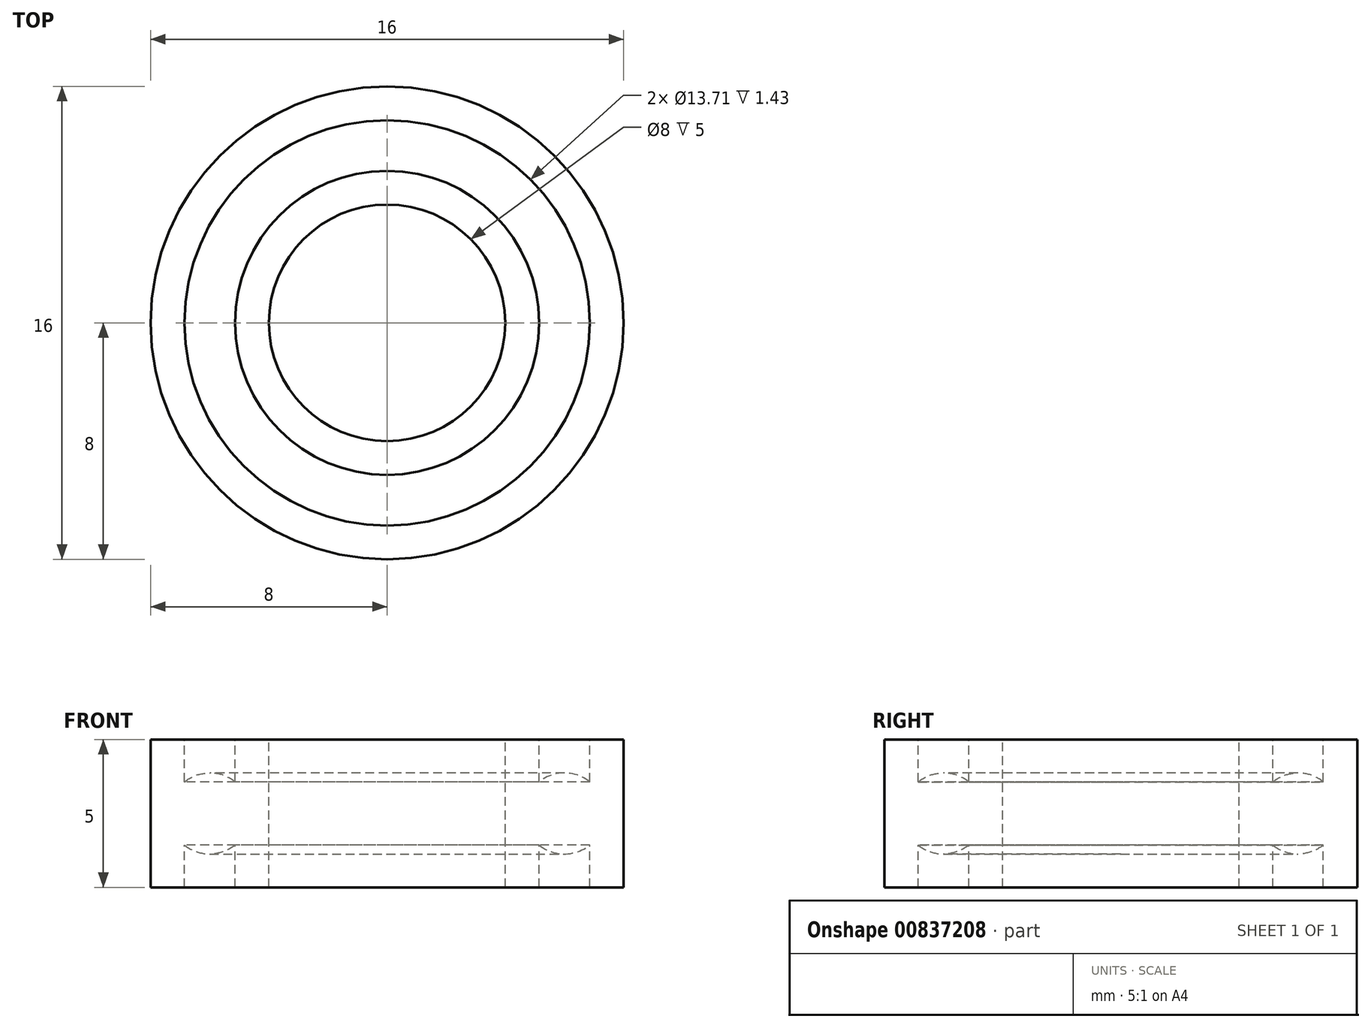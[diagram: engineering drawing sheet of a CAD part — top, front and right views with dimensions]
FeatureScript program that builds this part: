
annotation { "Feature Type Name" : "Feature", "Feature Type Description" : "" }
export const myFeature = defineFeature(function(context is Context, id is Id, definition is map)
    precondition{}
    {
        {
            var Q0;
            Q0=qCreatedBy(makeId("Front.planeOp"),FACE);
            var sketch = newSketch(context, id + "F0", { "sketchPlane" : qUnion([Q0])});
            skLineSegment(sketch, "E0.bottom", {"start": v(-8, 5) * mm, "end": v(-6.86, 5) * mm});
            skLineSegment(sketch, "E0.top", {"start": v(-8, 0) * mm, "end": v(-6.86, 0) * mm});
            skLineSegment(sketch, "E0.left", {"start": v(-8, 5) * mm, "end": v(-8, 0) * mm});
            skLineSegment(sketch, "E0.right", {"start": v(-4, 5) * mm, "end": v(-4, 0) * mm});
            skLineSegment(sketch, "E1", {"start": v(-8, 5) * mm, "end": v(-4, 0) * mm, "construction": true});
            skLineSegment(sketch, "E2", {"start": v(-4, 5) * mm, "end": v(-8, 0) * mm, "construction": true});
            skArc(sketch, "E3", {"start": v(-5.14, 3.57) * mm, "mid": v(-6, 3.87) * mm, "end": v(-6.86, 3.57) * mm});
            skLineSegment(sketch, "E4", {"start": v(-6.86, 3.57) * mm, "end": v(-6.86, 5) * mm});
            skLineSegment(sketch, "E5", {"start": v(-5.14, 3.57) * mm, "end": v(-5.14, 5) * mm});
            skLineSegment(sketch, "E6", {"start": v(-6.86, 1.43) * mm, "end": v(-6.86, 0) * mm});
            skLineSegment(sketch, "E7", {"start": v(-5.14, 1.43) * mm, "end": v(-5.14, 0) * mm});
            skLineSegment(sketch, "E8.trimOffspring", {"start": v(-5.14, 5) * mm, "end": v(-4, 5) * mm});
            skArc(sketch, "E9.trimOffspring", {"start": v(-6.86, 1.43) * mm, "mid": v(-6, 1.13) * mm, "end": v(-5.14, 1.43) * mm});
            skLineSegment(sketch, "E10.trimOffspring", {"start": v(-5.14, 0) * mm, "end": v(-4, 0) * mm});
            skLineSegment(sketch, "E11", {"start": v(0, 8.03) * mm, "end": v(0, -4.24) * mm, "construction": true});
            skSolve(sketch);
        }
        {
            var Q0;
            Q0=makeQuery(id+"F0.imprint","IMPRINT",FACE,{"disambiguationData":[TD([[makeQuery(id+"F0.imprint","IMPRINT",EDGE,{"derivedFrom":sQuery(id+"F0.wireOp",EDGE,"E0.bottom")}),-1.0]])]});
            var Q1;
            Q1 = qConstructionFilter(qBodyType(qCreatedBy(id + "F0" ,EDGE), BodyType.WIRE), ConstructionObject.NO);
            var Q2;
            Q2=sQuery(id+"F0.wireOp",EDGE,"E11");
            revolve(context, id + "F1", {"surfaceOperationType" : NewSurfaceOperationType.NEW, "entities" : qUnion([Q0]), "surfaceEntities" : qUnion([Q1]), "axis" : qUnion([Q2]), "revolveType" : RevolveType.FULL});
        }
    });
